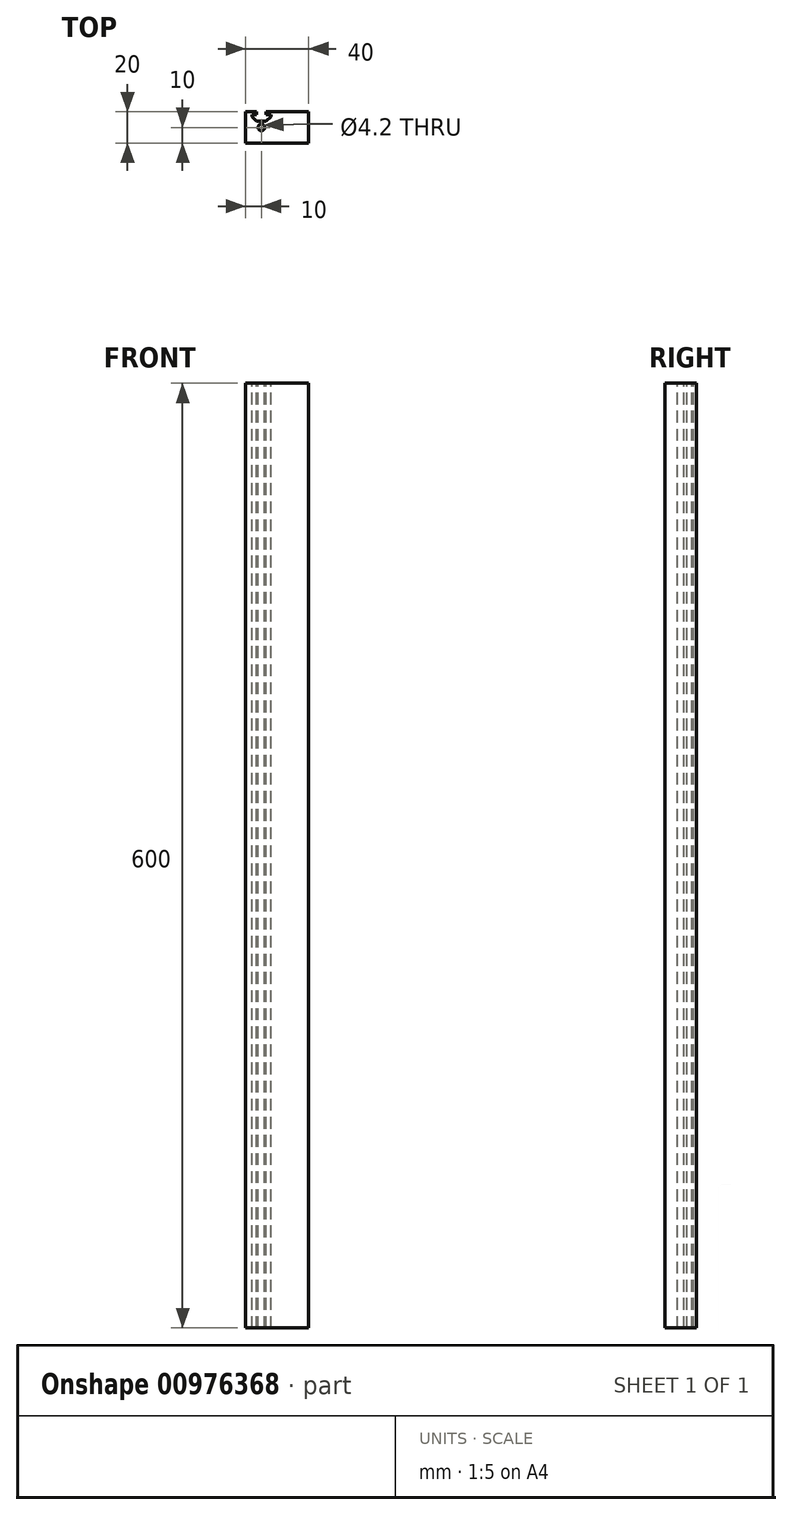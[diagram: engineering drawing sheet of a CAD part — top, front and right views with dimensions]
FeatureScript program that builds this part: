
annotation { "Feature Type Name" : "Feature", "Feature Type Description" : "" }
export const myFeature = defineFeature(function(context is Context, id is Id, definition is map)
    precondition{}
    {
        {
            var Q0;
            Q0=qCreatedBy(makeId("Top.planeOp"),FACE);
            var sketch = newSketch(context, id + "F0", { "sketchPlane" : qUnion([Q0])});
            skLineSegment(sketch, "E0.bottom", {"start": v(20, -10) * mm, "end": v(-20, -10) * mm});
            skLineSegment(sketch, "E0.top", {"start": v(20, 10) * mm, "end": v(-20, 10) * mm});
            skLineSegment(sketch, "E0.left", {"start": v(20, -10) * mm, "end": v(20, 10) * mm});
            skLineSegment(sketch, "E0.right", {"start": v(-20, -10) * mm, "end": v(-20, 10) * mm});
            skPoint(sketch, "E0.middle", {"position": v(0, 0) * mm});
            skSolve(sketch);
        }
        {
            var Q0;
            Q0 = qSketchRegion(id + "F0", true);
            extrude(context, id + "F1", {"entities" : qUnion([Q0]), "endBound" : BoundingType.SYMMETRIC, "depth" : 600 * mm, "offsetDistance" : 25 * mm});
        }
        {
            var Q0;
            Q0=makeQuery(id+"F1.opExtrude","CAP_FACE",FACE,{"disambiguationData":[OSD([sQuery(id+"F0.wireOp",EDGE,"E0.bottom"),sQuery(id+"F0.wireOp",EDGE,"E0.top"),sQuery(id+"F0.wireOp",EDGE,"E0.left"),sQuery(id+"F0.wireOp",EDGE,"E0.right")])],"isStart":false});
            var sketch = newSketch(context, id + "F2", { "sketchPlane" : qUnion([Q0])});
            skLineSegment(sketch, "E1", {"start": v(-13, 10) * mm, "end": v(-7, 10) * mm});
            skLineSegment(sketch, "E2", {"start": v(-7, 10) * mm, "end": v(-7, 8) * mm});
            skLineSegment(sketch, "E3", {"start": v(-7, 8) * mm, "end": v(-4, 8) * mm});
            skLineSegment(sketch, "E4", {"start": v(-4, 8) * mm, "end": v(-4, 7) * mm});
            skLineSegment(sketch, "E5", {"start": v(-4, 7) * mm, "end": v(-7, 4) * mm});
            skLineSegment(sketch, "E6", {"start": v(-7, 4) * mm, "end": v(-13, 4) * mm});
            skLineSegment(sketch, "E7", {"start": v(-13, 4) * mm, "end": v(-16, 7) * mm});
            skLineSegment(sketch, "E8", {"start": v(-16, 7) * mm, "end": v(-16, 8) * mm});
            skLineSegment(sketch, "E9", {"start": v(-16, 8) * mm, "end": v(-13, 8) * mm});
            skLineSegment(sketch, "E10", {"start": v(-13, 8) * mm, "end": v(-13, 10) * mm});
            skPoint(sketch, "E11", {"position": v(-10, 10) * mm});
            skPoint(sketch, "E12", {"position": v(-10, 4) * mm});
            skSolve(sketch);
        }
        {
            var Q0;
            Q0 = qSketchRegion(id + "F2", true);
            extrude(context, id + "F3", {"entities" : qUnion([Q0]), "operationType" : NewBodyOperationType.REMOVE, "endBound" : BoundingType.THROUGH_ALL, "oppositeDirection" : true, "depth" : 25 * mm, "offsetDistance" : 25 * mm});
        }
        {
            var Q0;
            Q0=makeQuery(id+"F1.opExtrude","CAP_FACE",FACE,{"disambiguationData":[OSD([sQuery(id+"F0.wireOp",EDGE,"E0.bottom"),sQuery(id+"F0.wireOp",EDGE,"E0.top"),sQuery(id+"F0.wireOp",EDGE,"E0.left"),sQuery(id+"F0.wireOp",EDGE,"E0.right")])],"isStart":false});
            var sketch = newSketch(context, id + "F4", { "sketchPlane" : qUnion([Q0])});
            skCircle(sketch, "E13", {"center": v(-10, 0) * mm, "radius": 2.1 * mm});
            skSolve(sketch);
        }
        {
            var Q0;
            Q0 = qSketchRegion(id + "F4", true);
            extrude(context, id + "F5", {"entities" : qUnion([Q0]), "operationType" : NewBodyOperationType.REMOVE, "endBound" : BoundingType.THROUGH_ALL, "oppositeDirection" : true, "depth" : 25 * mm, "offsetDistance" : 25 * mm});
        }
    });
